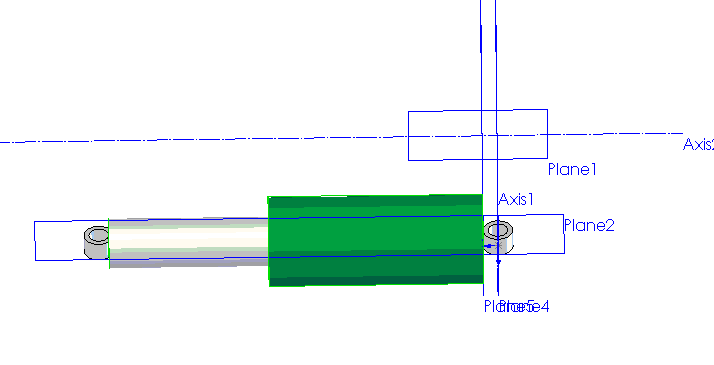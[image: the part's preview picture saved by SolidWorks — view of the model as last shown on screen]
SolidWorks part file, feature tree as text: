
SOLIDWORKS PART (.sldprt)
format: sldprt  version: not decoded by parser v0  size: 161,280 bytes
history: native  units: mm
features: plane x4, sketch x3, extrude x3, cut_extrude x1 (+11 scaffold rows collapsed)
feature tree (22):
  scaffold x11  (default folders/planes/origin — collapsed)
  sketch  "Sketch1"  dims[D1=19.05mm D2=19.05mm D3=12.7mm D4=12.7mm D5=254.0mm]
  extrude  "Extrude1"  Depth=12.7mm
  plane  "Plane1"  Offset=76.2mm
  plane  "Plane2"
  extrude  "Axis2"  [1 undecoded]
  plane  "Plane4"
  plane  "Plane5"  Offset=9.525mm
  sketch  "Sketch2"  dims[D1=57.15mm]
  extrude  "Extrude2"  Depth=238.125mm
  sketch  "Sketch3"  dims[D1=31.75mm]
  cut_extrude  "Cut-Extrude1"  Depth=101.6mm
decode coverage: 6 of 7 modeling features carry decoded parameters
note: 1 parameter value undecoded
note: suppression state not decoded; provenance and decode notes live in map.json
